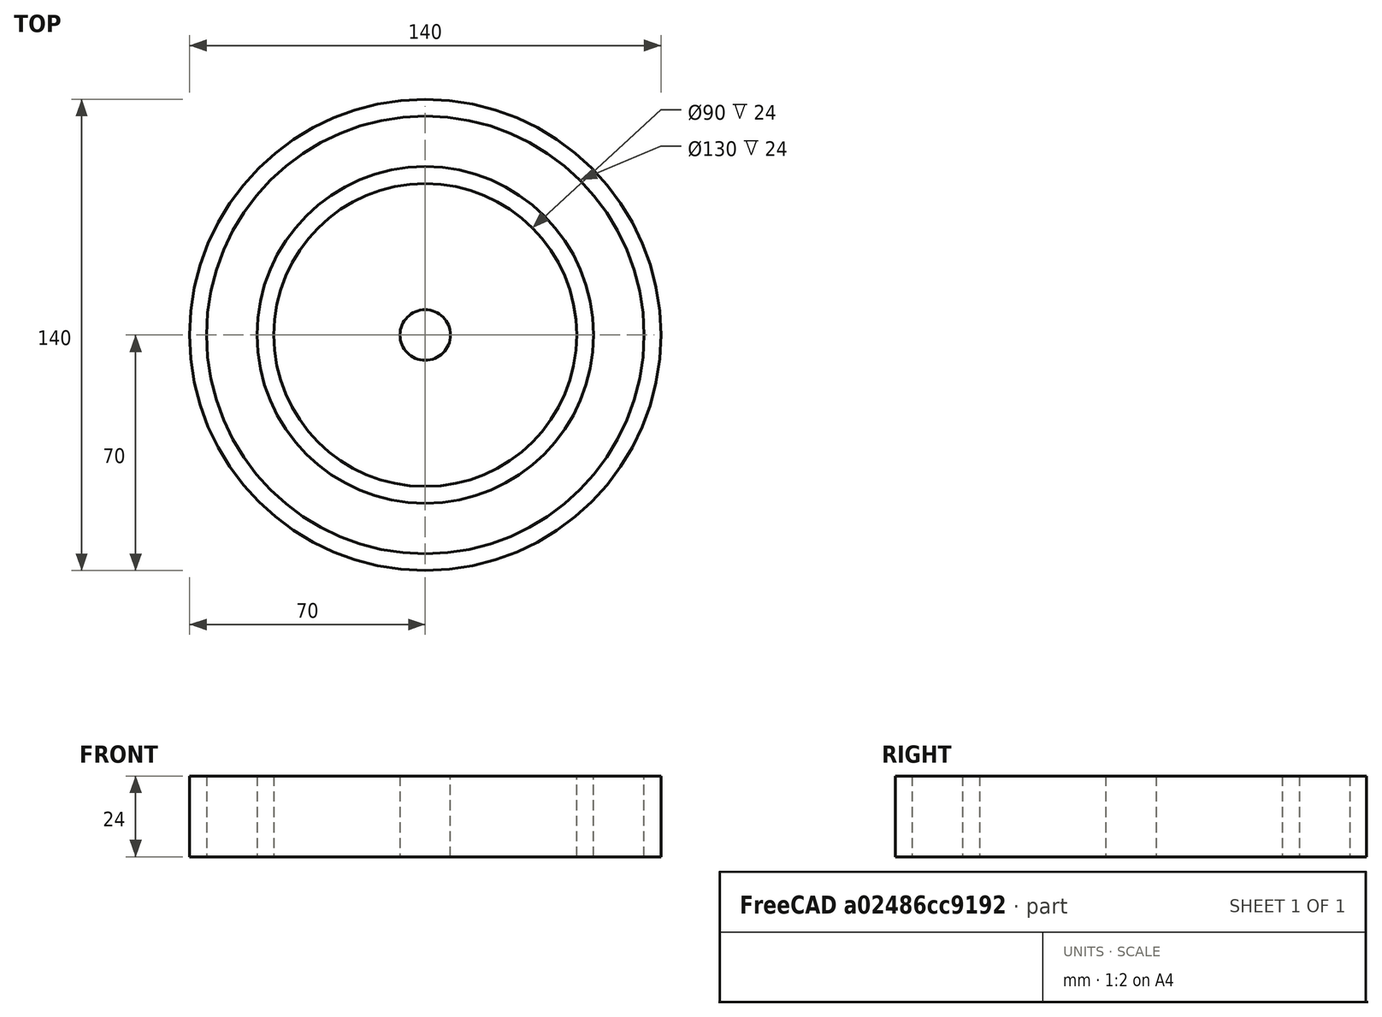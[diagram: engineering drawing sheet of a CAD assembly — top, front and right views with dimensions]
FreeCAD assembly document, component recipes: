
FREECAD ASSEMBLY — COMPONENT RECIPES ("Assambly_bearing_90x140x24")

This assembly document has 4 components, labeled P0..P3 below (a component is one placed body or linked part). 3 of them carry a construction recipe — the FreeCAD feature program that regenerates the part from scratch, quoted from this document or its linked companion documents; the rest are supplied as boundary geometry only. No exploded tour is included for this assembly.
COMPONENT P0 — geometry summary ("Assembly"; no construction recipe available for this part):
  bounding box: 140.0 x 140.0 x 24.0 mm
  tessellated surface: 208 triangles
  volume: 4160000000000000998637095284951213116179811637890312246504315009050071130092835195972460412616514207744 mm^3 (884353741496598776588298660686335503579452507655159701867829570910008133984476323021233100609814528% of its bounding box)
  symmetry: 2-fold rotationally symmetric about the x axis; 2-fold rotationally symmetric about the y axis; 4-fold rotationally symmetric about the z axis; mirror-symmetric across its x mid-plane, y mid-plane, z mid-plane
COMPONENT P1 — recipe-attached ("Body_ring_in", modeled in this document).
Construction recipe (the document's own serialized feature program — sketch geometry with constraints, then the solid features built on it; lengths are millimeters unless a unit is written):

FEATURE [Sketcher::SketchObject] Sketch
  FullyConstrained = true
  MapMode = 5
  Support = -> [XY_Plane001]
  sketch-geometry (2):
    g0: Circle CenterX=0 CenterY=0 CenterZ=0 NormalX=0 NormalY=0 NormalZ=1 AngleXU=0 Radius=50
    g1: Circle CenterX=0 CenterY=0 CenterZ=0 NormalX=0 NormalY=0 NormalZ=1 AngleXU=0 Radius=45
  constraints (4):
    c: Coincident(g1,g0)
    c: Diameter(g1) = 90
    c: Diameter(g0) = 100
    c: Coincident(g0,g-1)
FEATURE [PartDesign::Pad] Pad
  Direction = (1,1,1)
  Length = 24
  Length2 = 100
  Profile = -> Sketch
  Type = 0
FEATURE [PartDesign::CoordinateSystem] LCS_ring_in
  AttacherType = Attacher::AttachEngine3D
  MapMode = 11
  Placement = pos=(0,0,24) rot=(0,0,1;1.5708rad)
  Support = -> [Pad]
FEATURE [PartDesign::Body] Body  label="Body_ring_in"
  Group = -> [Sketch,Pad,LCS_ring_in]
  Origin = -> Origin001
  Tip = -> Pad
COMPONENT P2 — recipe-attached ("Body_ring_out", modeled in this document).
Construction recipe (the document's own serialized feature program — sketch geometry with constraints, then the solid features built on it; lengths are millimeters unless a unit is written):

FEATURE [Sketcher::SketchObject] Sketch001
  FullyConstrained = true
  MapMode = 5
  Support = -> [XY_Plane002]
  sketch-geometry (2):
    g0: Circle CenterX=0 CenterY=0 CenterZ=0 NormalX=0 NormalY=0 NormalZ=1 AngleXU=0 Radius=65
    g1: Circle CenterX=0 CenterY=0 CenterZ=0 NormalX=0 NormalY=0 NormalZ=1 AngleXU=0 Radius=70
  constraints (4):
    c: Coincident(g1,g0)
    c: Diameter(g1) = 140
    c: Diameter(g0) = 130
    c: Coincident(g0,g-1)
FEATURE [PartDesign::Pad] Pad001
  Direction = (1,1,1)
  Length = 24
  Length2 = 100
  Profile = -> Sketch001
  Type = 0
FEATURE [PartDesign::CoordinateSystem] LCS_ring_out
  AttacherType = Attacher::AttachEngine3D
  MapMode = 11
  Placement = pos=(0,0,24) rot=(0,0,1;1.5708rad)
  Support = -> [Pad001]
FEATURE [PartDesign::Body] Body001  label="Body_ring_out"
  Group = -> [Sketch001,Pad001,LCS_ring_out]
  Origin = -> Origin002
  Tip = -> Pad001
COMPONENT P3 — recipe-attached ("Body_roller", modeled in this document).
Construction recipe (the document's own serialized feature program — sketch geometry with constraints, then the solid features built on it; lengths are millimeters unless a unit is written):

FEATURE [Sketcher::SketchObject] Sketch002
  FullyConstrained = true
  MapMode = 5
  Support = -> [XY_Plane003]
  sketch-geometry (1):
    g0: Circle CenterX=0 CenterY=0 CenterZ=0 NormalX=0 NormalY=0 NormalZ=1 AngleXU=0 Radius=7.5
  constraints (2):
    c: Diameter(g0) = 15
    c: Coincident(g0,g-1)
FEATURE [PartDesign::Pad] Pad002
  Direction = (1,1,1)
  Length = 24
  Length2 = 100
  Profile = -> Sketch002
  Type = 0
FEATURE [PartDesign::CoordinateSystem] LCS_R1
  AttacherType = Attacher::AttachEngine3D
  MapMode = 5
  Placement = pos=(0,0,24) rot=(0,0,1;0rad)
  Support = -> [Pad002]
FEATURE [PartDesign::Body] Body002  label="Body_roller"
  Group = -> [Sketch002,Pad002,LCS_R1]
  Origin = -> Origin003
  Tip = -> Pad002
PROVENANCE & LICENSES
A FreeCAD (.FCStd) document from a public repository crawl; recipes are the document's own serialized feature recipes (and, for linked parts, companion documents' recipes).
License: as declared in the source repository (recorded in the dataset sidecar).
